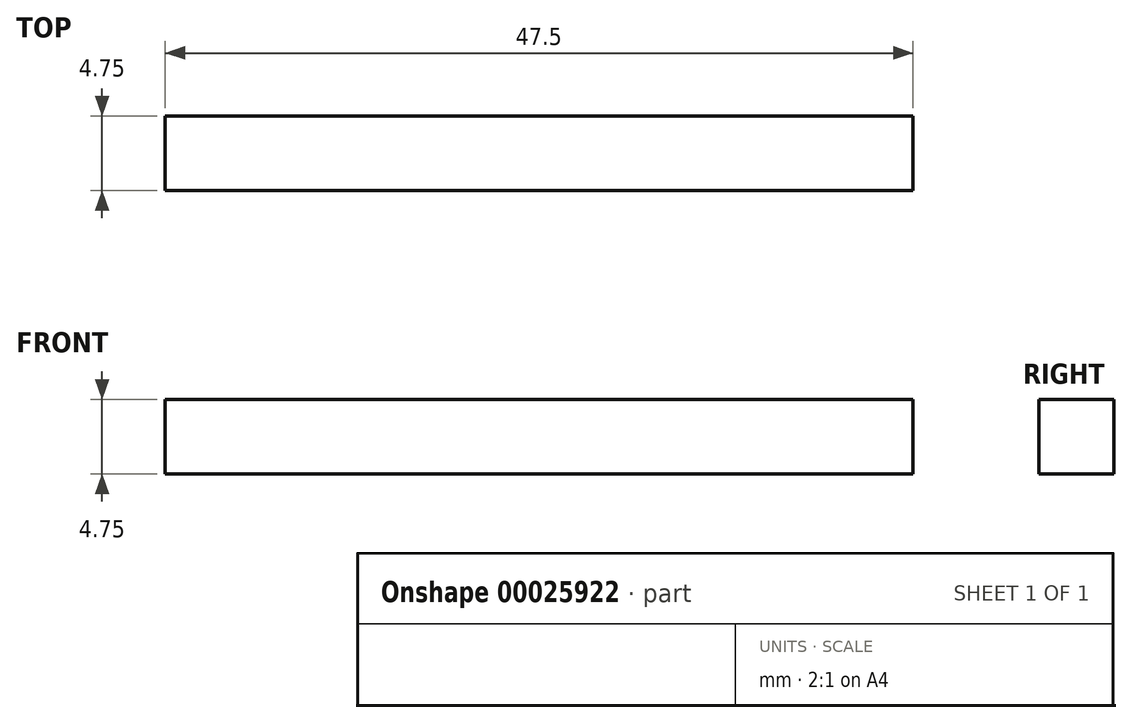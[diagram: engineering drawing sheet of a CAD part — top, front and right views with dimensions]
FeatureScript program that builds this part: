
annotation { "Feature Type Name" : "Feature", "Feature Type Description" : "" }
export const myFeature = defineFeature(function(context is Context, id is Id, definition is map)
    precondition{}
    {
        {
            var Q0;
            Q0=qCreatedBy(makeId("Front.planeOp"),FACE);
            var sketch = newSketch(context, id + "F0", { "sketchPlane" : qUnion([Q0])});
            skLineSegment(sketch, "E0.bottom", {"start": v(0, 0) * mm, "end": v(47.5, 0) * mm});
            skLineSegment(sketch, "E0.top", {"start": v(0, 4.75) * mm, "end": v(47.5, 4.75) * mm});
            skLineSegment(sketch, "E0.left", {"start": v(0, 0) * mm, "end": v(0, 4.75) * mm});
            skLineSegment(sketch, "E0.right", {"start": v(47.5, 0) * mm, "end": v(47.5, 4.75) * mm});
            skSolve(sketch);
        }
        {
            var Q0;
            Q0=makeQuery(id+"F0.imprint","IMPRINT",FACE,{"disambiguationData":[TD([[makeQuery(id+"F0.imprint","IMPRINT",EDGE,{"derivedFrom":sQuery(id+"F0.wireOp",EDGE,"E0.bottom")}),1.0]])]});
            extrude(context, id + "F1", {"entities" : qUnion([Q0]), "depth" : 4.75 * mm});
        }
    });
